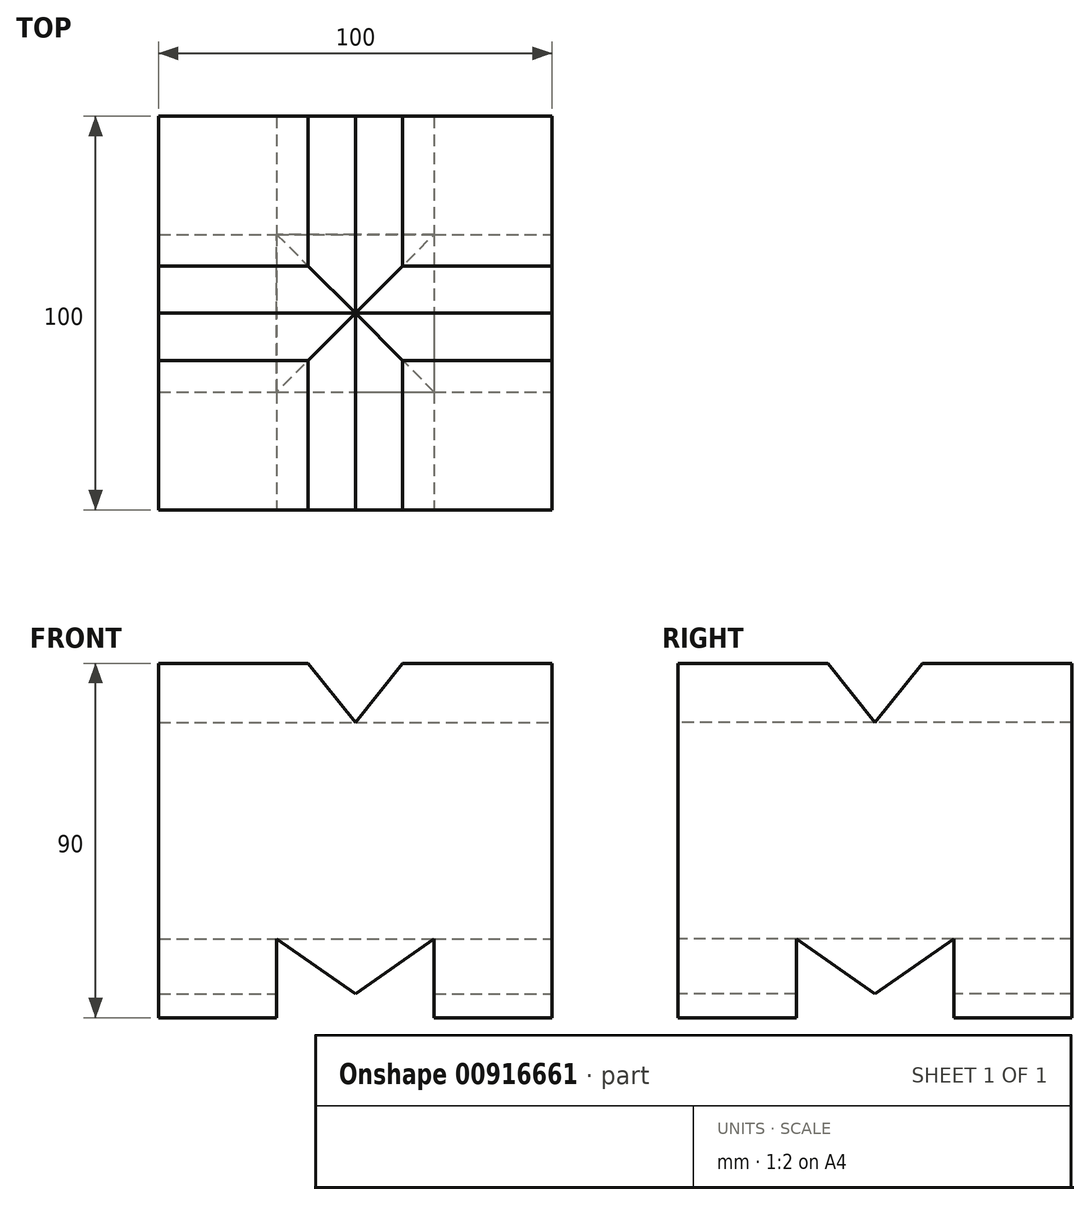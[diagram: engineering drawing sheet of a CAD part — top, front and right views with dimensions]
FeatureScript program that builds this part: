
annotation { "Feature Type Name" : "Feature", "Feature Type Description" : "" }
export const myFeature = defineFeature(function(context is Context, id is Id, definition is map)
    precondition{}
    {
        {
            var Q0;
            Q0=qCreatedBy(makeId("Top.planeOp"),FACE);
            var sketch = newSketch(context, id + "F0", { "sketchPlane" : qUnion([Q0])});
            skLineSegment(sketch, "E0.bottom", {"start": v(-50, -50) * mm, "end": v(50, -50) * mm});
            skLineSegment(sketch, "E0.top", {"start": v(-50, 50) * mm, "end": v(50, 50) * mm});
            skLineSegment(sketch, "E0.left", {"start": v(-50, -50) * mm, "end": v(-50, 50) * mm});
            skLineSegment(sketch, "E0.right", {"start": v(50, -50) * mm, "end": v(50, 50) * mm});
            skPoint(sketch, "E0.middle", {"position": v(0, 0) * mm});
            skSolve(sketch);
        }
        {
            var Q0;
            Q0 = qSketchRegion(id + "F0", true);
            extrude(context, id + "F1", {"entities" : qUnion([Q0]), "depth" : 90 * mm, "offsetDistance" : 25 * mm});
        }
        {
            var Q0;
            Q0=makeQuery(id+"F1.opExtrude","SWEPT_FACE",FACE,{"disambiguationData":[OSD([sQuery(id+"F0.wireOp",EDGE,"E0.bottom")])]});
            var sketch = newSketch(context, id + "F2", { "sketchPlane" : qUnion([Q0])});
            skLineSegment(sketch, "E1", {"start": v(-20, 0) * mm, "end": v(-20, 20) * mm});
            skLineSegment(sketch, "E2", {"start": v(20, 20) * mm, "end": v(20, 0) * mm});
            skLineSegment(sketch, "E3", {"start": v(-20, 0) * mm, "end": v(20, 0) * mm});
            skLineSegment(sketch, "E4", {"start": v(-20, 20) * mm, "end": v(0, 6) * mm});
            skLineSegment(sketch, "E5", {"start": v(0, 6) * mm, "end": v(20, 20) * mm});
            skSolve(sketch);
        }
        {
            var Q0;
            Q0 = qSketchRegion(id + "F2", true);
            extrude(context, id + "F3", {"entities" : qUnion([Q0]), "operationType" : NewBodyOperationType.REMOVE, "endBound" : BoundingType.THROUGH_ALL, "oppositeDirection" : true, "depth" : 25 * mm, "offsetDistance" : 25 * mm});
        }
        {
            var Q0;
            Q0=makeQuery(id+"F1.opExtrude","SWEPT_FACE",FACE,{"disambiguationData":[OSD([sQuery(id+"F0.wireOp",EDGE,"E0.right")])]});
            var sketch = newSketch(context, id + "F4", { "sketchPlane" : qUnion([Q0])});
            skLineSegment(sketch, "E6", {"start": v(-20, 0) * mm, "end": v(-20, 20) * mm});
            skLineSegment(sketch, "E7", {"start": v(20, 20) * mm, "end": v(20, 0) * mm});
            skLineSegment(sketch, "E8", {"start": v(20, 0) * mm, "end": v(-20, 0) * mm});
            skLineSegment(sketch, "E9", {"start": v(-20, 20) * mm, "end": v(0, 6) * mm});
            skLineSegment(sketch, "E10", {"start": v(0, 6) * mm, "end": v(20, 20) * mm});
            skSolve(sketch);
        }
        {
            var Q0;
            Q0 = qSketchRegion(id + "F4", true);
            extrude(context, id + "F5", {"entities" : qUnion([Q0]), "operationType" : NewBodyOperationType.REMOVE, "endBound" : BoundingType.THROUGH_ALL, "oppositeDirection" : true, "depth" : 25 * mm, "offsetDistance" : 25 * mm});
        }
        {
            var Q0;
            Q0=makeQuery(id+"F1.opExtrude","SWEPT_FACE",FACE,{"disambiguationData":[OSD([sQuery(id+"F0.wireOp",EDGE,"E0.right")])]});
            var sketch = newSketch(context, id + "F6", { "sketchPlane" : qUnion([Q0])});
            skLineSegment(sketch, "E11", {"start": v(-12, 90) * mm, "end": v(0, 75) * mm});
            skLineSegment(sketch, "E12", {"start": v(0, 75) * mm, "end": v(12, 90) * mm});
            skLineSegment(sketch, "E13", {"start": v(12, 90) * mm, "end": v(-12, 90) * mm});
            skSolve(sketch);
        }
        {
            var Q0;
            Q0 = qSketchRegion(id + "F6", true);
            extrude(context, id + "F7", {"entities" : qUnion([Q0]), "operationType" : NewBodyOperationType.REMOVE, "endBound" : BoundingType.THROUGH_ALL, "oppositeDirection" : true, "depth" : 25 * mm, "offsetDistance" : 25 * mm});
        }
        {
            var Q0;
            Q0=makeQuery(id+"F1.opExtrude","SWEPT_FACE",FACE,{"disambiguationData":[OSD([sQuery(id+"F0.wireOp",EDGE,"E0.bottom")])]});
            var sketch = newSketch(context, id + "F8", { "sketchPlane" : qUnion([Q0])});
            skLineSegment(sketch, "E14", {"start": v(-12, 90) * mm, "end": v(0, 75) * mm});
            skLineSegment(sketch, "E15", {"start": v(0, 75) * mm, "end": v(12, 90) * mm});
            skLineSegment(sketch, "E16", {"start": v(12, 90) * mm, "end": v(-12, 90) * mm});
            skSolve(sketch);
        }
        {
            var Q0;
            Q0 = qSketchRegion(id + "F8", true);
            extrude(context, id + "F9", {"entities" : qUnion([Q0]), "operationType" : NewBodyOperationType.REMOVE, "endBound" : BoundingType.THROUGH_ALL, "oppositeDirection" : true, "depth" : 25 * mm, "offsetDistance" : 25 * mm});
        }
    });
